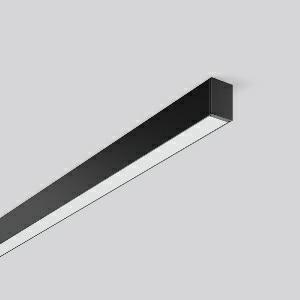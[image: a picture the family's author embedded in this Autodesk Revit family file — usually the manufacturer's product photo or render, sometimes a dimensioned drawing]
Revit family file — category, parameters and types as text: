
# Revit family: less_is_more_27_312196_003_1_76_acd7
name_source: partatom
category: Lighting Fixtures
units: mm (PartAtom-declared; Revit-internal decimal feet)

## family parameters
Cut with Voids When Loaded = No
Host = Face
Light Source = No
Part Type = Normal
Room Calculation Point = No
Round Connector Dimension = Use Diameter
Shared = No

## types (1)
- LESS IS MORE 27 (1 x LED Modul 840, 1600 lm, 4000)
    Apparent Load = 25 VA
    CIE Flux Codes = 48 79 96 100 100
    Color Rendering = 80
    Color Temperature = 4000
    Default Elevation = 1800 mm
    Description = Series: LESS IS MORE 27
Ceiling and wall luminaire with slim design. Housing: extruded aluminium profile, powder-coated. End cap aluminium powder-coated. Diffuser made of non-yellowing plastic (PMMA), opal. Suitable for Ceiling mounting, Wall (surface). External driver with connecting cable. 
Colour: deep black, matt (RAL 9005)
Length: 1012 mm
Width: 28 mm
Height: 38 mm
Lamp: LED
Socket: without socket
Colour temperature: 4000K
Colour rendering index (CRI): 82
System power: 25 W
Rated luminous flux: 1600 lm
Luminous efficiency: 64 lm/W
Control gear: Voltage converter, DALI dim.
Protection class: II
Type of protection: IP 20
    Height = 38 mm
    Lamp = 1 x LED Modul 840
    Lamp Light Flux = 1600 lm
    Lamp count = 1
    Length = 1012 mm
    Lifetime = 50000 h
    Luminous efficacy = 64 lm/W
    Manufacturer = RZB
    ModVariant = No
    Model = 312196.003.1.76
    Mounting Place = Ceiling, Wall
    Mounting Type = Surface mounted
    Number of Poles = 1
    OnlyDefault = Yes
    Power Factor = 1
    Product Name = LESS IS MORE 27
    Product group = Surface mounted LED linear luminaires
    ProductGroupID = 307
    Protection Class = Protection class II
    Protection Degree = IP 20
    RLX_Detail_Level = 1
    RLX_Emergency_Light_Flux = 0 lm
    RLX_Emergency_Type = 0
    RLX_Emergency_Type_DB = No
    RlxData = <blob elided: 28665 chars, md5=9ab3a89f>
    Socket = socket
    Standby Power = 0 W
    System Light Flux = 1600 lm
    System Power = 25 W
    Type Comments = Product without accessories
    Type Image = 312196.003.jpg
    URL = http://relux.com
    VarID = ---
    Voltage = 230 V
    Voltage Range = 220-240 V
    Weight = 0.00 kg
    Width = 28 mm

## geometry (parser evidence)
native form markers: Blend x4, Sweep x10
no freeform markers — native parametric forms only
